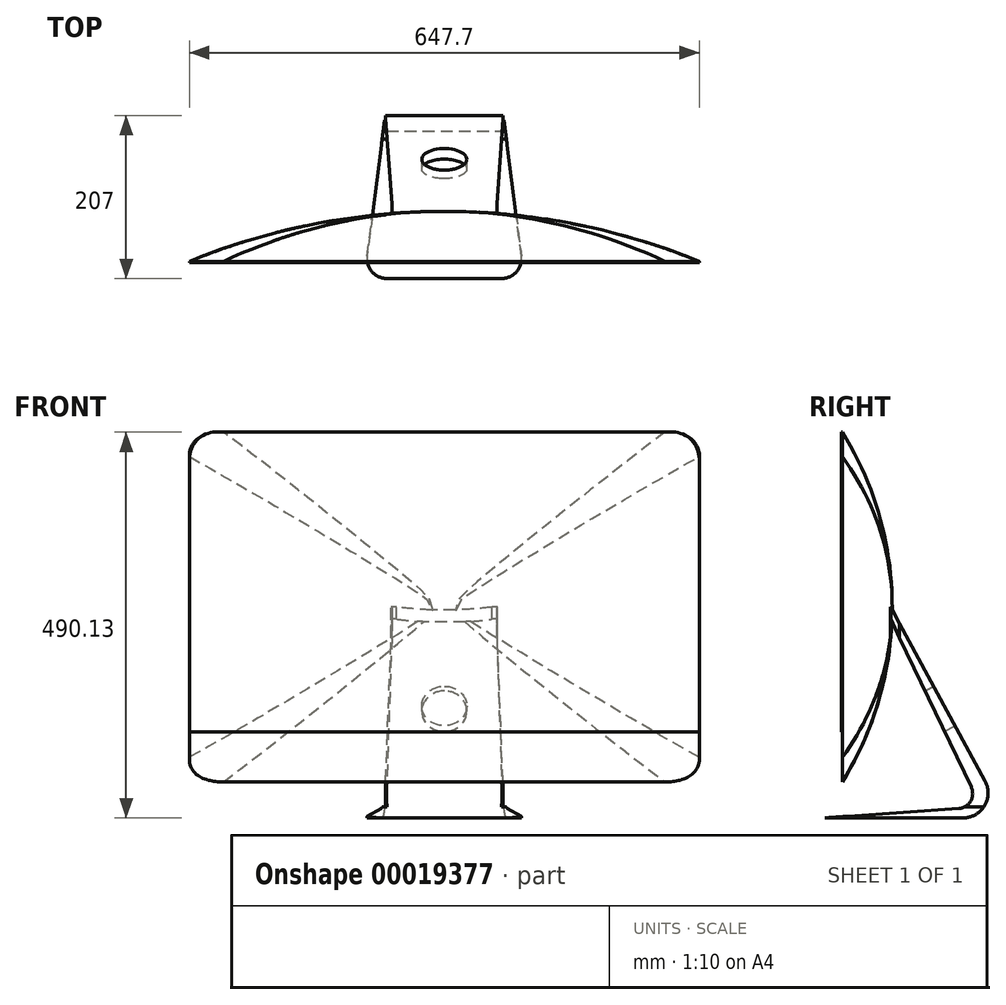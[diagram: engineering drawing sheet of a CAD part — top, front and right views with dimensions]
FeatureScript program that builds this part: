
annotation { "Feature Type Name" : "Feature", "Feature Type Description" : "" }
export const myFeature = defineFeature(function(context is Context, id is Id, definition is map)
    precondition{}
    {
        {
            var Q0;
            Q0=qCreatedBy(makeId("Right.planeOp"),FACE);
            var sketch = newSketch(context, id + "F0", { "sketchPlane" : qUnion([Q0])});
            skLineSegment(sketch, "E0.rect.right", {"start": v(-31.75, 222.25) * mm, "end": v(-31.75, -222.25) * mm});
            skPoint(sketch, "E0.rect.middle", {"position": v(0, 0) * mm});
            skPoint(sketch, "E1", {"position": v(-31.75, 0) * mm});
            skPoint(sketch, "E2", {"position": v(31.75, 0) * mm});
            skLineSegment(sketch, "E3", {"start": v(-31.75, 0) * mm, "end": v(31.75, 0) * mm, "construction": true});
            skArc(sketch, "E4", {"start": v(-31.75, -222.25) * mm, "mid": v(31.75, 0) * mm, "end": v(-31.75, 222.25) * mm});
            skPoint(sketch, "E5.orphan", {"position": v(31.75, -222.25) * mm});
            skPoint(sketch, "E0.rect.bottom.start.orphan", {"position": v(31.75, 222.25) * mm});
            skSolve(sketch);
        }
        {
            var Q0;
            Q0 = qSketchRegion(id + "F0", true);
            extrude(context, id + "F1", {"entities" : qUnion([Q0]), "endBound" : BoundingType.SYMMETRIC, "depth" : 647.7 * mm});
        }
        {
            var Q0;
            Q0=qCreatedBy(makeId("Top.planeOp"),FACE);
            var sketch = newSketch(context, id + "F2", { "sketchPlane" : qUnion([Q0])});
            skPoint(sketch, "E6", {"position": v(0, -31.64) * mm});
            skPoint(sketch, "E7", {"position": v(0, 31.86) * mm});
            skPoint(sketch, "E8", {"position": v(-323.85, -31.64) * mm});
            skPoint(sketch, "E9", {"position": v(-323.85, 31.86) * mm});
            skPoint(sketch, "E10", {"position": v(323.85, -31.64) * mm});
            skPoint(sketch, "E11", {"position": v(323.85, 31.86) * mm});
            skArc(sketch, "E12", {"start": v(323.85, -31.64) * mm, "mid": v(0, 31.86) * mm, "end": v(-323.85, -31.64) * mm});
            skLineSegment(sketch, "E13", {"start": v(-323.85, -31.64) * mm, "end": v(-323.85, 31.86) * mm});
            skLineSegment(sketch, "E14", {"start": v(-323.85, 31.86) * mm, "end": v(0, 31.86) * mm});
            skLineSegment(sketch, "E15", {"start": v(323.85, 31.86) * mm, "end": v(0, 31.86) * mm});
            skLineSegment(sketch, "E16", {"start": v(323.85, -31.64) * mm, "end": v(323.85, 31.86) * mm});
            skSolve(sketch);
        }
        {
            var Q0;
            Q0 = qSketchRegion(id + "F2", true);
            extrude(context, id + "F3", {"entities" : qUnion([Q0]), "operationType" : NewBodyOperationType.REMOVE, "endBound" : BoundingType.SYMMETRIC, "oppositeDirection" : true, "depth" : 444.5 * mm});
        }
        {
            var Q0;
            {var subQ0=sQuery(id+"F2.wireOp",EDGE,"E12");Q0=makeQuery(id+"F3.boolean.opBoolean","INTERSECT",EDGE,{"derivedFrom":[makeQuery(id+"F1.opExtrude","SWEPT_FACE",FACE,{"disambiguationData":[OSD([sQuery(id+"F0.wireOp",EDGE,"E4")])]}),makeQuery(id+"F3.opExtrude","SWEPT_FACE",FACE,{"disambiguationData":[OSD([subQ0]),TDD([makeQuery(id+"F2.imprint","IMPRINT",EDGE,{"disambiguationData":[TD([[makeQuery(id+"F2.imprint","INTERSECT",VERTEX,{"derivedFrom":[subQ0,sQuery(id+"F2.wireOp",EDGE,"E16")]}),-1.0]])],"derivedFrom":subQ0})])]})]});}
            var Q1;
            {var subQ0=sQuery(id+"F2.wireOp",EDGE,"E12");Q1=makeQuery(id+"F3.boolean.opBoolean","INTERSECT",EDGE,{"derivedFrom":[makeQuery(id+"F1.opExtrude","SWEPT_FACE",FACE,{"disambiguationData":[OSD([sQuery(id+"F0.wireOp",EDGE,"E4")])]}),makeQuery(id+"F3.opExtrude","SWEPT_FACE",FACE,{"disambiguationData":[OSD([subQ0]),TDD([makeQuery(id+"F2.imprint","IMPRINT",EDGE,{"disambiguationData":[TD([[makeQuery(id+"F2.imprint","INTERSECT",VERTEX,{"derivedFrom":[subQ0,sQuery(id+"F2.wireOp",EDGE,"E13")]}),1.0]])],"derivedFrom":subQ0})])]})]});}
            fillet(context, id + "F4", {"entities" : qUnion([Q0, Q1]), "radius" : 76.2 * mm, "tangentPropagation" : true, "allowEdgeOverflow" : false});
        }
        {
            var Q0;
            Q0=qCreatedBy(makeId("Right.planeOp"),FACE);
            var sketch = newSketch(context, id + "F5", { "sketchPlane" : qUnion([Q0])});
            skPoint(sketch, "E17", {"position": v(29.74, 0) * mm});
            skLineSegment(sketch, "E18", {"start": v(29.74, 0) * mm, "end": v(175.13, -267.88) * mm});
            skLineSegment(sketch, "E19", {"start": v(175.13, -267.88) * mm, "end": v(-53.47, -267.88) * mm});
            skLineSegment(sketch, "E20", {"start": v(-53.47, -267.88) * mm, "end": v(144.14, -254.06) * mm});
            skLineSegment(sketch, "E21", {"start": v(144.14, -254.06) * mm, "end": v(29.74, -15.3) * mm});
            skLineSegment(sketch, "E22", {"start": v(29.74, -15.3) * mm, "end": v(29.74, 0) * mm});
            skSolve(sketch);
        }
        {
            var Q0;
            Q0 = qSketchRegion(id + "F5", true);
            extrude(context, id + "F6", {"entities" : qUnion([Q0]), "operationType" : NewBodyOperationType.ADD, "endBound" : BoundingType.SYMMETRIC, "depth" : 203.2 * mm});
        }
        {
            var Q0;
            Q0=qCreatedBy(makeId("Top.planeOp"),FACE);
            var sketch = newSketch(context, id + "F7", { "sketchPlane" : qUnion([Q0])});
            skLineSegment(sketch, "E23", {"start": v(-66.68, 41.16) * mm, "end": v(-104.23, 41.16) * mm});
            skLineSegment(sketch, "E24", {"start": v(-104.23, 41.16) * mm, "end": v(-104.23, 174.47) * mm});
            skLineSegment(sketch, "E25", {"start": v(-104.23, 174.47) * mm, "end": v(-76.29, 174.47) * mm});
            skLineSegment(sketch, "E26", {"start": v(-76.29, 174.47) * mm, "end": v(-104.23, 174.47) * mm});
            skLineSegment(sketch, "E27", {"start": v(-76.29, 174.47) * mm, "end": v(-66.68, 41.16) * mm});
            skLineSegment(sketch, "E28", {"start": v(66.68, 41.16) * mm, "end": v(104.23, 41.16) * mm});
            skLineSegment(sketch, "E29", {"start": v(104.23, 41.16) * mm, "end": v(104.23, 174.47) * mm});
            skLineSegment(sketch, "E30", {"start": v(104.23, 174.47) * mm, "end": v(76.29, 174.47) * mm});
            skLineSegment(sketch, "E31", {"start": v(76.29, 174.47) * mm, "end": v(66.68, 41.16) * mm});
            skPoint(sketch, "E32.end.orphan", {"position": v(0, 41.16) * mm});
            skSolve(sketch);
        }
        {
            var Q0;
            Q0 = qSketchRegion(id + "F7", true);
            extrude(context, id + "F8", {"entities" : qUnion([Q0]), "operationType" : NewBodyOperationType.REMOVE, "oppositeDirection" : true, "depth" : 254 * mm});
        }
        {
            var Q0;
            Q0=makeQuery(id+"F6.opExtrude","SWEPT_FACE",FACE,{"disambiguationData":[OSD([sQuery(id+"F5.wireOp",EDGE,"E19")])]});
            var sketch = newSketch(context, id + "F9", { "sketchPlane" : qUnion([Q0])});
            skLineSegment(sketch, "E33", {"start": v(-101.6, 53.47) * mm, "end": v(101.6, 53.47) * mm});
            skLineSegment(sketch, "E34", {"start": v(101.6, 53.47) * mm, "end": v(101.6, -175.13) * mm});
            skLineSegment(sketch, "E35", {"start": v(101.6, -175.13) * mm, "end": v(101.6, 53.47) * mm});
            skLineSegment(sketch, "E36", {"start": v(-101.6, 53.47) * mm, "end": v(-101.6, -175.13) * mm});
            skLineSegment(sketch, "E37", {"start": v(-101.6, -175.13) * mm, "end": v(-72.39, -175.13) * mm});
            skLineSegment(sketch, "E38", {"start": v(-101.6, 53.47) * mm, "end": v(-72.4, -175.13) * mm});
            skLineSegment(sketch, "E39", {"start": v(101.6, -175.13) * mm, "end": v(72.4, -175.13) * mm});
            skLineSegment(sketch, "E40", {"start": v(72.4, -175.13) * mm, "end": v(101.6, 53.47) * mm});
            skSolve(sketch);
        }
        {
            var Q0;
            Q0 = qSketchRegion(id + "F9", true);
            extrude(context, id + "F10", {"entities" : qUnion([Q0]), "operationType" : NewBodyOperationType.REMOVE, "oppositeDirection" : true, "depth" : 18.23 * mm});
        }
        {
            var Q0;
            Q0=makeQuery(id+"F8.boolean.opBoolean","COPY",FACE,{"derivedFrom":makeQuery(id+"F8.opExtrude","SWEPT_FACE",FACE,{"disambiguationData":[OSD([sQuery(id+"F7.wireOp",EDGE,"E28")])]})});
            var sketch = newSketch(context, id + "F11", { "sketchPlane" : qUnion([Q0])});
            skLineSegment(sketch, "E41", {"start": v(-101.6, -39.14) * mm, "end": v(-101.6, 0) * mm});
            skLineSegment(sketch, "E42", {"start": v(-101.6, 0) * mm, "end": v(-66.68, 0) * mm});
            skLineSegment(sketch, "E43", {"start": v(-66.68, 0) * mm, "end": v(-66.68, -39.14) * mm});
            skLineSegment(sketch, "E44", {"start": v(-66.68, -39.14) * mm, "end": v(-101.6, -39.14) * mm});
            skSolve(sketch);
        }
        {
            var Q0;
            Q0 = qSketchRegion(id + "F11", true);
            extrude(context, id + "F12", {"entities" : qUnion([Q0]), "operationType" : NewBodyOperationType.REMOVE, "oppositeDirection" : true, "depth" : 11.94 * mm});
        }
        {
            var Q0;
            Q0=makeQuery(id+"F8.boolean.opBoolean","COPY",FACE,{"derivedFrom":makeQuery(id+"F8.opExtrude","SWEPT_FACE",FACE,{"disambiguationData":[OSD([sQuery(id+"F7.wireOp",EDGE,"E23")])]})});
            var sketch = newSketch(context, id + "F13", { "sketchPlane" : qUnion([Q0])});
            skLineSegment(sketch, "E45", {"start": v(101.6, -39.14) * mm, "end": v(101.6, 0) * mm});
            skLineSegment(sketch, "E46", {"start": v(101.6, -39.14) * mm, "end": v(66.67, -39.14) * mm});
            skLineSegment(sketch, "E47", {"start": v(66.67, -39.14) * mm, "end": v(66.67, 0) * mm});
            skLineSegment(sketch, "E48", {"start": v(66.67, 0) * mm, "end": v(101.6, 0) * mm});
            skSolve(sketch);
        }
        {
            var Q0;
            {var subQ1=sQuery(id+"F13.wireOp",EDGE,"E48");Q0=makeQuery(id+"F13.imprint","IMPRINT",FACE,{"disambiguationData":[TD([[makeQuery(id+"F13.imprint","IMPRINT",EDGE,{"derivedFrom":subQ1}),-1.0]])]});}
            var Q1;
            {var subQ2=sQuery(id+"F13.wireOp",EDGE,"E46");Q1=makeQuery(id+"F13.imprint","IMPRINT",FACE,{"disambiguationData":[TD([[makeQuery(id+"F13.imprint","IMPRINT",EDGE,{"derivedFrom":subQ2}),-1.0]])]});}
            extrude(context, id + "F14", {"entities" : qUnion([Q0, Q1]), "operationType" : NewBodyOperationType.REMOVE, "oppositeDirection" : true, "depth" : 11.95 * mm});
        }
        {
            var Q0;
            Q0=makeQuery(id+"F6.opExtrude","SWEPT_EDGE",EDGE,{"disambiguationData":[OSD([sQuery(id+"F5.wireOp",EDGE,"E20"),sQuery(id+"F5.wireOp",EDGE,"E21")])]});
            fillet(context, id + "F15", {"entities" : qUnion([Q0]), "radius" : 19.05 * mm, "tangentPropagation" : true, "allowEdgeOverflow" : false});
        }
        {
            var Q0;
            Q0=makeQuery(id+"F6.opExtrude","SWEPT_EDGE",EDGE,{"disambiguationData":[OSD([sQuery(id+"F5.wireOp",EDGE,"E18"),sQuery(id+"F5.wireOp",EDGE,"E19")])]});
            fillet(context, id + "F16", {"entities" : qUnion([Q0]), "radius" : 31.75 * mm, "tangentPropagation" : true, "allowEdgeOverflow" : false});
        }
        {
            var Q0;
            Q0=makeQuery(id+"F6.opExtrude","SWEPT_FACE",FACE,{"disambiguationData":[OSD([sQuery(id+"F5.wireOp",EDGE,"E19")])]});
            var sketch = newSketch(context, id + "F17", { "sketchPlane" : qUnion([Q0])});
            skPoint(sketch, "E49.visualSharp", {"position": v(-101.6, 53.47) * mm});
            skArc(sketch, "E49.filletArc", {"start": v(-72.75, 53.47) * mm, "mid": v(-91.81, 44.85) * mm, "end": v(-97.94, 24.85) * mm});
            skPoint(sketch, "E50.visualSharp", {"position": v(101.6, 53.47) * mm});
            skArc(sketch, "E50.filletArc", {"start": v(97.94, 24.85) * mm, "mid": v(91.81, 44.85) * mm, "end": v(72.75, 53.47) * mm});
            skLineSegment(sketch, "E51", {"start": v(-97.94, 24.85) * mm, "end": v(-101.6, 53.47) * mm});
            skLineSegment(sketch, "E52", {"start": v(-72.75, 53.47) * mm, "end": v(-101.6, 53.47) * mm});
            skLineSegment(sketch, "E53", {"start": v(72.75, 53.47) * mm, "end": v(101.6, 53.47) * mm});
            skLineSegment(sketch, "E54", {"start": v(97.94, 24.85) * mm, "end": v(101.6, 53.47) * mm});
            skSolve(sketch);
        }
        {
            var Q0;
            Q0 = qSketchRegion(id + "F17", true);
            extrude(context, id + "F18", {"entities" : qUnion([Q0]), "operationType" : NewBodyOperationType.REMOVE, "oppositeDirection" : true, "depth" : 12.7 * mm});
        }
        {
            var Q0;
            Q0=makeQuery(id+"F1.opExtrude","SWEPT_FACE",FACE,{"disambiguationData":[OSD([sQuery(id+"F0.wireOp",EDGE,"E0.rect.right")])]});
            var sketch = newSketch(context, id + "F19", { "sketchPlane" : qUnion([Q0])});
            skLineSegment(sketch, "E55", {"start": v(323.85, -158.75) * mm, "end": v(323.85, 188.42) * mm});
            skLineSegment(sketch, "E56", {"start": v(290.02, 222.25) * mm, "end": v(-289.9, 222.25) * mm});
            skLineSegment(sketch, "E57", {"start": v(-323.85, 188.3) * mm, "end": v(-323.85, -158.75) * mm});
            skPoint(sketch, "E58.end.orphan", {"position": v(-323.85, -222.25) * mm});
            skPoint(sketch, "E58.start.orphan", {"position": v(323.85, -222.25) * mm});
            skLineSegment(sketch, "E59", {"start": v(-323.85, -158.75) * mm, "end": v(323.85, -158.75) * mm});
            skPoint(sketch, "E60.visualSharp", {"position": v(-323.85, 222.25) * mm});
            skArc(sketch, "E60.filletArc", {"start": v(-289.9, 222.25) * mm, "mid": v(-313.9, 212.3) * mm, "end": v(-323.85, 188.3) * mm});
            skPoint(sketch, "E61.visualSharp", {"position": v(323.85, 222.25) * mm});
            skArc(sketch, "E61.filletArc", {"start": v(323.85, 188.42) * mm, "mid": v(313.94, 212.34) * mm, "end": v(290.02, 222.25) * mm});
            skSolve(sketch);
        }
        {
            var Q0;
            Q0 = qSketchRegion(id + "F19", true);
            extrude(context, id + "F20", {"entities" : qUnion([Q0]), "operationType" : NewBodyOperationType.ADD, "depth" : 1.27 * mm});
        }
        {
            var Q0;
            Q0=makeQuery(id+"F6.opExtrude","SWEPT_FACE",FACE,{"disambiguationData":[OSD([sQuery(id+"F5.wireOp",EDGE,"E18")])]});
            var sketch = newSketch(context, id + "F21", { "sketchPlane" : qUnion([Q0])});
            skCircle(sketch, "E62", {"center": v(0, -157.29) * mm, "radius": 28.58 * mm});
            skSolve(sketch);
        }
        {
            var Q0;
            Q0 = qSketchRegion(id + "F21", true);
            extrude(context, id + "F22", {"entities" : qUnion([Q0]), "operationType" : NewBodyOperationType.REMOVE, "oppositeDirection" : true, "depth" : 25.4 * mm});
        }
    });
